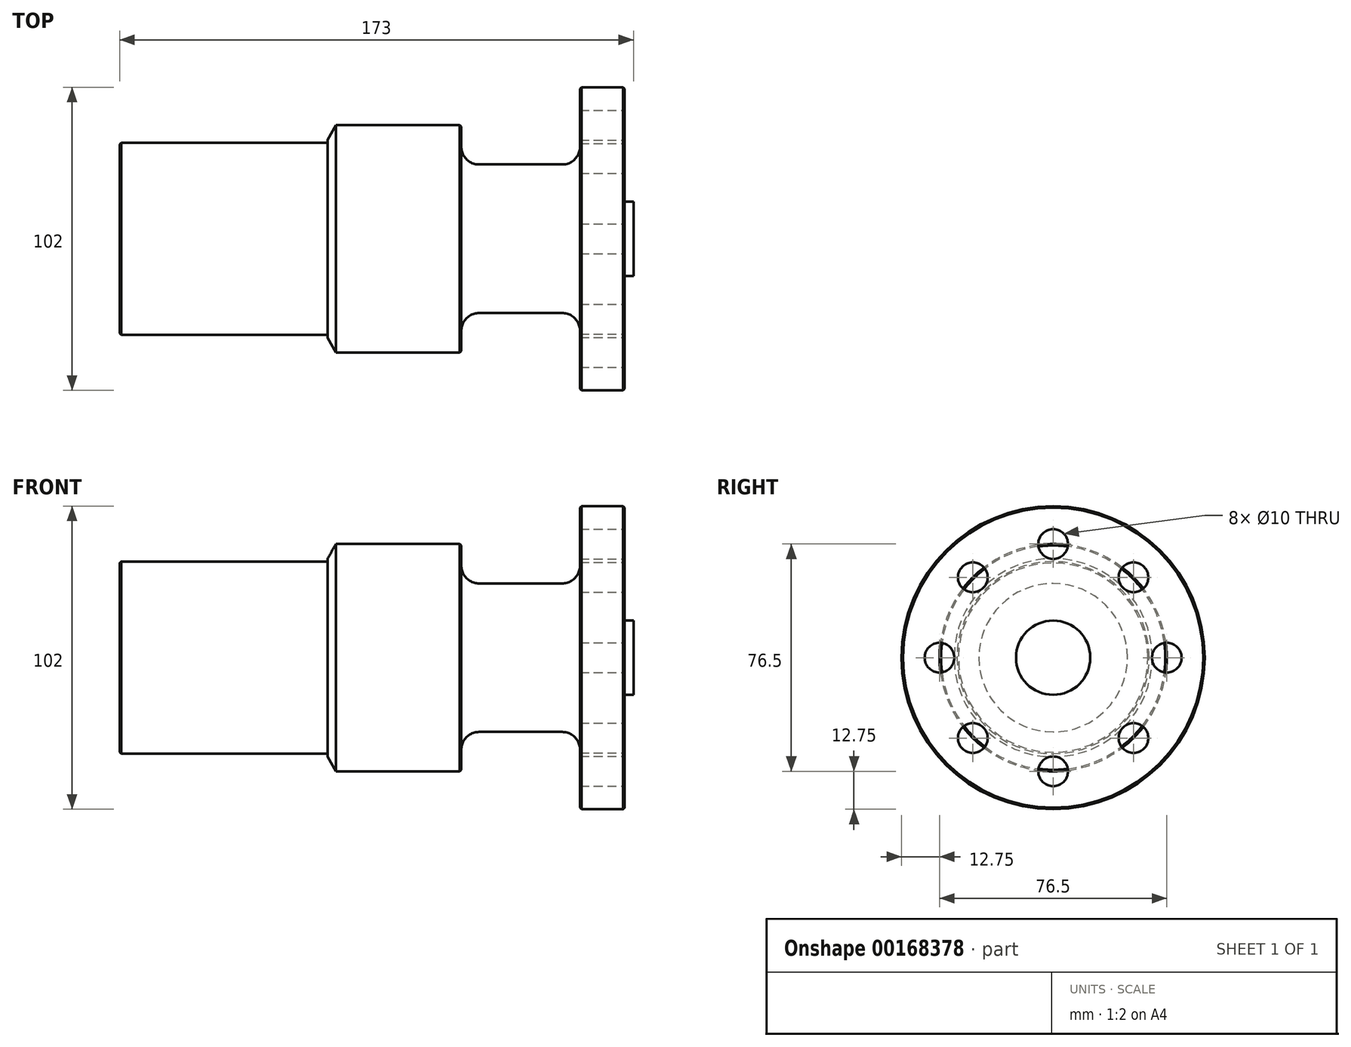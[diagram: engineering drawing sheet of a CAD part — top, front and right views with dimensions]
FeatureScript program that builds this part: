
annotation { "Feature Type Name" : "Feature", "Feature Type Description" : "" }
export const myFeature = defineFeature(function(context is Context, id is Id, definition is map)
    precondition{}
    {
        {
            var Q0;
            Q0=qCreatedBy(makeId("Front.planeOp"),FACE);
            var sketch = newSketch(context, id + "F0", { "sketchPlane" : qUnion([Q0])});
            skLineSegment(sketch, "E0", {"start": v(0, 0) * mm, "end": v(0, 32.35) * mm});
            skLineSegment(sketch, "E1", {"start": v(0, 32.35) * mm, "end": v(70, 32.35) * mm});
            skLineSegment(sketch, "E2", {"start": v(72.83, 38.25) * mm, "end": v(115, 38.25) * mm});
            skLineSegment(sketch, "E3", {"start": v(115, 38.25) * mm, "end": v(115, 31) * mm});
            skLineSegment(sketch, "E4", {"start": v(121, 25) * mm, "end": v(149, 25) * mm});
            skLineSegment(sketch, "E5", {"start": v(155, 31) * mm, "end": v(155, 51) * mm});
            skLineSegment(sketch, "E6", {"start": v(155, 51) * mm, "end": v(170, 51) * mm});
            skLineSegment(sketch, "E7", {"start": v(173, 12.5) * mm, "end": v(173, 0) * mm});
            skLineSegment(sketch, "E8", {"start": v(0, 0) * mm, "end": v(173, 0) * mm});
            skLineSegment(sketch, "E9", {"start": v(170, 51) * mm, "end": v(170, 12.5) * mm});
            skLineSegment(sketch, "E10", {"start": v(170, 12.5) * mm, "end": v(173, 12.5) * mm});
            skLineSegment(sketch, "E11", {"start": v(70, 32.35) * mm, "end": v(70, 33.35) * mm});
            skLineSegment(sketch, "E12", {"start": v(70, 33.35) * mm, "end": v(72.83, 38.25) * mm});
            skPoint(sketch, "E13.visualSharp", {"position": v(115, 25) * mm});
            skArc(sketch, "E13.filletArc", {"start": v(115, 31) * mm, "mid": v(116.76, 26.76) * mm, "end": v(121, 25) * mm});
            skPoint(sketch, "E14.visualSharp", {"position": v(155, 25) * mm});
            skArc(sketch, "E14.filletArc", {"start": v(149, 25) * mm, "mid": v(153.24, 26.76) * mm, "end": v(155, 31) * mm});
            skSolve(sketch);
        }
        {
            var Q0;
            Q0=makeQuery(id+"F0.imprint","IMPRINT",FACE,{"disambiguationData":[TD([[makeQuery(id+"F0.imprint","IMPRINT",EDGE,{"derivedFrom":sQuery(id+"F0.wireOp",EDGE,"E0")}),-1.0]])]});
            var Q1;
            Q1=sQuery(id+"F0.wireOp",EDGE,"E8");
            revolve(context, id + "F1", {"entities" : qUnion([Q0]), "axis" : qUnion([Q1]), "revolveType" : RevolveType.FULL});
        }
        {
            var Q0;
            Q0=makeQuery(id+"F1.opRevolve","SWEPT_EDGE",EDGE,{"disambiguationData":[OSD([sQuery(id+"F0.wireOp",EDGE,"E0"),sQuery(id+"F0.wireOp",EDGE,"E1")])]});
            var Q1;
            Q1=makeQuery(id+"F1.opRevolve","SWEPT_EDGE",EDGE,{"disambiguationData":[OSD([sQuery(id+"F0.wireOp",EDGE,"E2"),sQuery(id+"F0.wireOp",EDGE,"E3")])]});
            var Q2;
            Q2=makeQuery(id+"F1.opRevolve","SWEPT_EDGE",EDGE,{"disambiguationData":[OSD([sQuery(id+"F0.wireOp",EDGE,"E5"),sQuery(id+"F0.wireOp",EDGE,"E6")])]});
            var Q3;
            Q3=makeQuery(id+"F1.opRevolve","SWEPT_EDGE",EDGE,{"disambiguationData":[OSD([sQuery(id+"F0.wireOp",EDGE,"E6"),sQuery(id+"F0.wireOp",EDGE,"E9")])]});
            chamfer(context, id + "F2", {"entities" : qUnion([Q0, Q1, Q2, Q3]), "width" : .5 * mm, "tangentPropagation" : true});
        }
        {
            var Q0;
            Q0=makeQuery(id+"F1.opRevolve","SWEPT_EDGE",EDGE,{"disambiguationData":[OSD([sQuery(id+"F0.wireOp",EDGE,"E1"),sQuery(id+"F0.wireOp",EDGE,"E11")])]});
            var Q1;
            Q1=makeQuery(id+"F1.opRevolve","SWEPT_EDGE",EDGE,{"disambiguationData":[OSD([sQuery(id+"F0.wireOp",EDGE,"E9"),sQuery(id+"F0.wireOp",EDGE,"E10")])]});
            fillet(context, id + "F3", {"entities" : qUnion([Q0, Q1]), "radius" : .5 * mm, "tangentPropagation" : true, "allowEdgeOverflow" : false});
        }
        {
            var Q0;
            Q0=makeQuery(id+"F1.opRevolve","SWEPT_FACE",FACE,{"disambiguationData":[OSD([sQuery(id+"F0.wireOp",EDGE,"E9")])]});
            var sketch = newSketch(context, id + "F4", { "sketchPlane" : qUnion([Q0])});
            skCircle(sketch, "E15", {"center": v(0, 38.25) * mm, "radius": 5 * mm});
            skCircle(sketch, "E16.1.0", {"center": v(-27.05, 27.05) * mm, "radius": 5 * mm});
            skCircle(sketch, "E16.2.0", {"center": v(-38.25, 0) * mm, "radius": 5 * mm});
            skCircle(sketch, "E16.3.0", {"center": v(-27.05, -27.05) * mm, "radius": 5 * mm});
            skCircle(sketch, "E16.4.0", {"center": v(0, -38.25) * mm, "radius": 5 * mm});
            skCircle(sketch, "E16.5.0", {"center": v(27.05, -27.05) * mm, "radius": 5 * mm});
            skCircle(sketch, "E16.6.0", {"center": v(38.25, 0) * mm, "radius": 5 * mm});
            skCircle(sketch, "E16.7.0", {"center": v(27.05, 27.05) * mm, "radius": 5 * mm});
            skPoint(sketch, "E16.center", {"position": v(0, 0) * mm});
            skSolve(sketch);
        }
        {
            var Q0;
            Q0 = qSketchRegion(id + "F4", true);
            var Q1;
            Q1=makeQuery(id+"F1.opRevolve","SWEPT_FACE",FACE,{"disambiguationData":[OSD([sQuery(id+"F0.wireOp",EDGE,"E5")])]});
            extrude(context, id + "F5", {"entities" : qUnion([Q0]), "operationType" : NewBodyOperationType.REMOVE, "endBound" : BoundingType.UP_TO_SURFACE, "oppositeDirection" : true, "endBoundEntityFace" : qUnion([Q1]), "depth" : 25 * mm});
        }
    });
